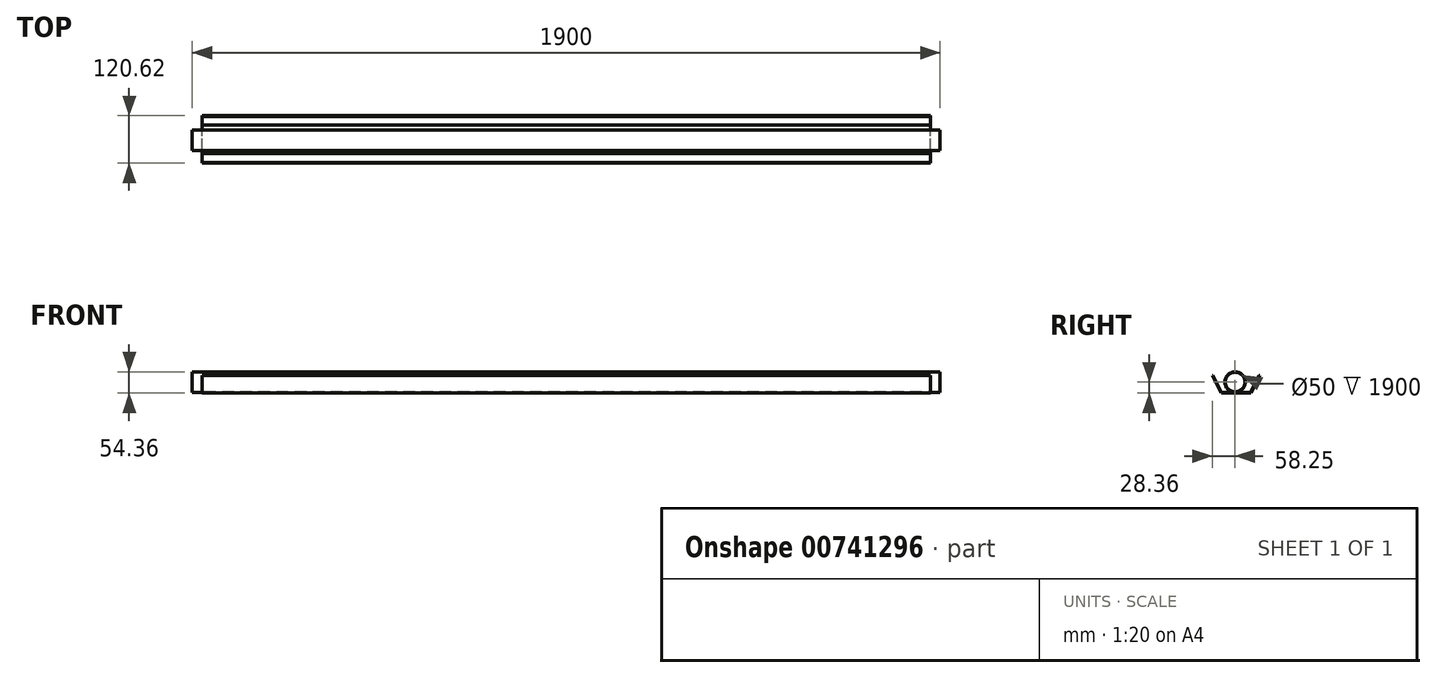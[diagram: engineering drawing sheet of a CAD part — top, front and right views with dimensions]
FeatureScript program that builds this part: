
annotation { "Feature Type Name" : "Feature", "Feature Type Description" : "" }
export const myFeature = defineFeature(function(context is Context, id is Id, definition is map)
    precondition{}
    {
        {
            var Q0;
            Q0=qCreatedBy(makeId("Right.planeOp"),FACE);
            var sketch = newSketch(context, id + "F0", { "sketchPlane" : qUnion([Q0])});
            skLineSegment(sketch, "E0", {"start": v(-35.44, -28.36) * mm, "end": v(39.56, -28.36) * mm});
            skLineSegment(sketch, "E1", {"start": v(-35.44, -28.36) * mm, "end": v(-58.25, 16.14) * mm});
            skLineSegment(sketch, "E2", {"start": v(-58.25, 16.14) * mm, "end": v(-56, 16.14) * mm});
            skLineSegment(sketch, "E3", {"start": v(62.37, 16.14) * mm, "end": v(39.56, -28.36) * mm});
            skLineSegment(sketch, "E4.0", {"start": v(-34.22, -26.36) * mm, "end": v(38.34, -26.36) * mm});
            skLineSegment(sketch, "E4.1", {"start": v(-34.22, -26.36) * mm, "end": v(-56, 16.14) * mm});
            skLineSegment(sketch, "E4.3", {"start": v(60.12, 16.14) * mm, "end": v(38.34, -26.36) * mm});
            skLineSegment(sketch, "E5.trimOffspring", {"start": v(60.12, 16.14) * mm, "end": v(62.37, 16.14) * mm});
            skSolve(sketch);
        }
        {
            var Q0;
            Q0=makeQuery(id+"F0.imprint","IMPRINT",FACE,{"disambiguationData":[TD([[makeQuery(id+"F0.imprint","IMPRINT",EDGE,{"derivedFrom":sQuery(id+"F0.wireOp",EDGE,"E0")}),1.0]])]});
            extrude(context, id + "F1", {"entities" : qUnion([Q0]), "endBound" : BoundingType.SYMMETRIC, "depth" : 1850 * mm, "offsetDistance" : 25 * mm});
        }
        {
            var Q0;
            Q0=qCreatedBy(makeId("Right.planeOp"),FACE);
            var sketch = newSketch(context, id + "F2", { "sketchPlane" : qUnion([Q0])});
            skCircle(sketch, "E6", {"center": v(0, 0) * mm, "radius": 26 * mm});
            skCircle(sketch, "E7", {"center": v(0, 0) * mm, "radius": 25 * mm});
            skSolve(sketch);
        }
        {
            var Q0;
            Q0=qSketchRegion(id+"F2",true);
            extrude(context, id + "F3", {"entities" : qUnion([Q0]), "endBound" : BoundingType.SYMMETRIC, "depth" : 1900 * mm, "offsetDistance" : 25 * mm});
        }
    });
